# Revit family: STH9607_30_40_65
name_source: partatom
category: Luminárias
units: mm (PartAtom-declared; Revit-internal decimal feet)

## family parameters
Com base no plano de trabalho = Não
Compartilhado = Não
Corte com vazios quando carregada = Não
Cota do conector redondo = Utilizar diâmetro
Fonte luminosa = Sim
Manter orientação da anotação = Não
Ponto de cálculo do ambiente = Não
Sempre na vertical = Sim
Tipo de parte = Normal

## types (3) — shared parameters
Comprimento = 0.6 m
Cromado = Cromado
Dimerização = Não dimerizável
Diâmetro = 0.03 m
Estrutura = Al - Branco
Fabricante = Stella
Filtro de cor = 16777215
Fluxo Luminoso = 900 lm
Grau de proteção (IP) = IP20
IRC (Índice de reprodução de cores) = >80
Modelo = Tubular T8 60cm
Potência = 9 W
Tensão Elétrica = 100V-240V
Troca de temperatura da cor de lâmpada com esmaecimento = <Nenhum>
URL = https://stella.com.br
Ângulo de Abertura = 200°
Ângulo de inclinação = 90.00°
zero-valued in all types: Elevação padrão

## per-type parameters (varying)
| type | Arquivo de rede fotométrica | Luminoso | Referência | Temperatura da cor (K) |
| STH9607/30 - BIVOLT - 3000K - 900lm - 200° | STELLA - STH9607-30 - TUBULAR T8 9W.ies | Luminoso - 3000K | STH9607/30 - BIVOLT | 3000 K |
| STH9607/40 - BIVOLT - 4000K - 900lm - 200° | STELLA - STH9607-40 - TUBULAR T8 9W.ies | Luminoso - 4000K | STH9607/40 - BIVOLT | 4000 K |
| STH9607/65 - BIVOLT - 6500K - 900lm - 200° | STELLA - STH9607-65 - TUBULAR T8 9W 60CM.ies | Luminoso - 6500K | STH9607/65 - BIVOLT | 6500 K |
